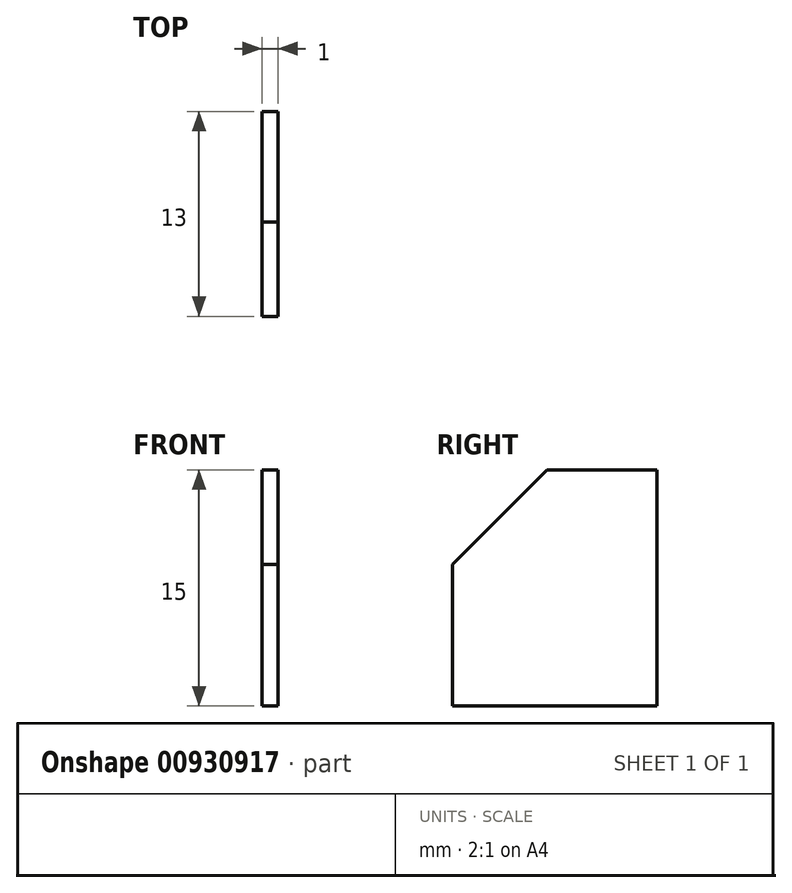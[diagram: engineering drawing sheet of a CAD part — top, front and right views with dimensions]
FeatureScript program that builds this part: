
annotation { "Feature Type Name" : "Feature", "Feature Type Description" : "" }
export const myFeature = defineFeature(function(context is Context, id is Id, definition is map)
    precondition{}
    {
        {
            var Q0;
            Q0=qCreatedBy(makeId("Right.planeOp"),FACE);
            var sketch = newSketch(context, id + "F0", { "sketchPlane" : qUnion([Q0])});
            skLineSegment(sketch, "E0.bottom", {"start": v(6.5, 7.5) * mm, "end": v(-0.5, 7.5) * mm});
            skLineSegment(sketch, "E0.top", {"start": v(6.5, -7.5) * mm, "end": v(-6.5, -7.5) * mm});
            skLineSegment(sketch, "E0.left", {"start": v(6.5, 7.5) * mm, "end": v(6.5, -7.5) * mm});
            skLineSegment(sketch, "E0.right", {"start": v(-6.5, 1.5) * mm, "end": v(-6.5, -7.5) * mm});
            skPoint(sketch, "E0.middle", {"position": v(0, 0) * mm});
            skLineSegment(sketch, "E1", {"start": v(-0.5, 7.5) * mm, "end": v(-6.5, 1.5) * mm});
            skPoint(sketch, "E2.orphan", {"position": v(-6.5, 7.5) * mm});
            skSolve(sketch);
        }
        {
            var Q0;
            Q0=makeQuery(id+"F0.imprint","IMPRINT",FACE,{"disambiguationData":[TD([[makeQuery(id+"F0.imprint","IMPRINT",EDGE,{"derivedFrom":sQuery(id+"F0.wireOp",EDGE,"E0.bottom")}),1.0]])]});
            extrude(context, id + "F1", {"entities" : qUnion([Q0]), "depth" : 1 * mm, "offsetDistance" : 25 * mm});
        }
    });
